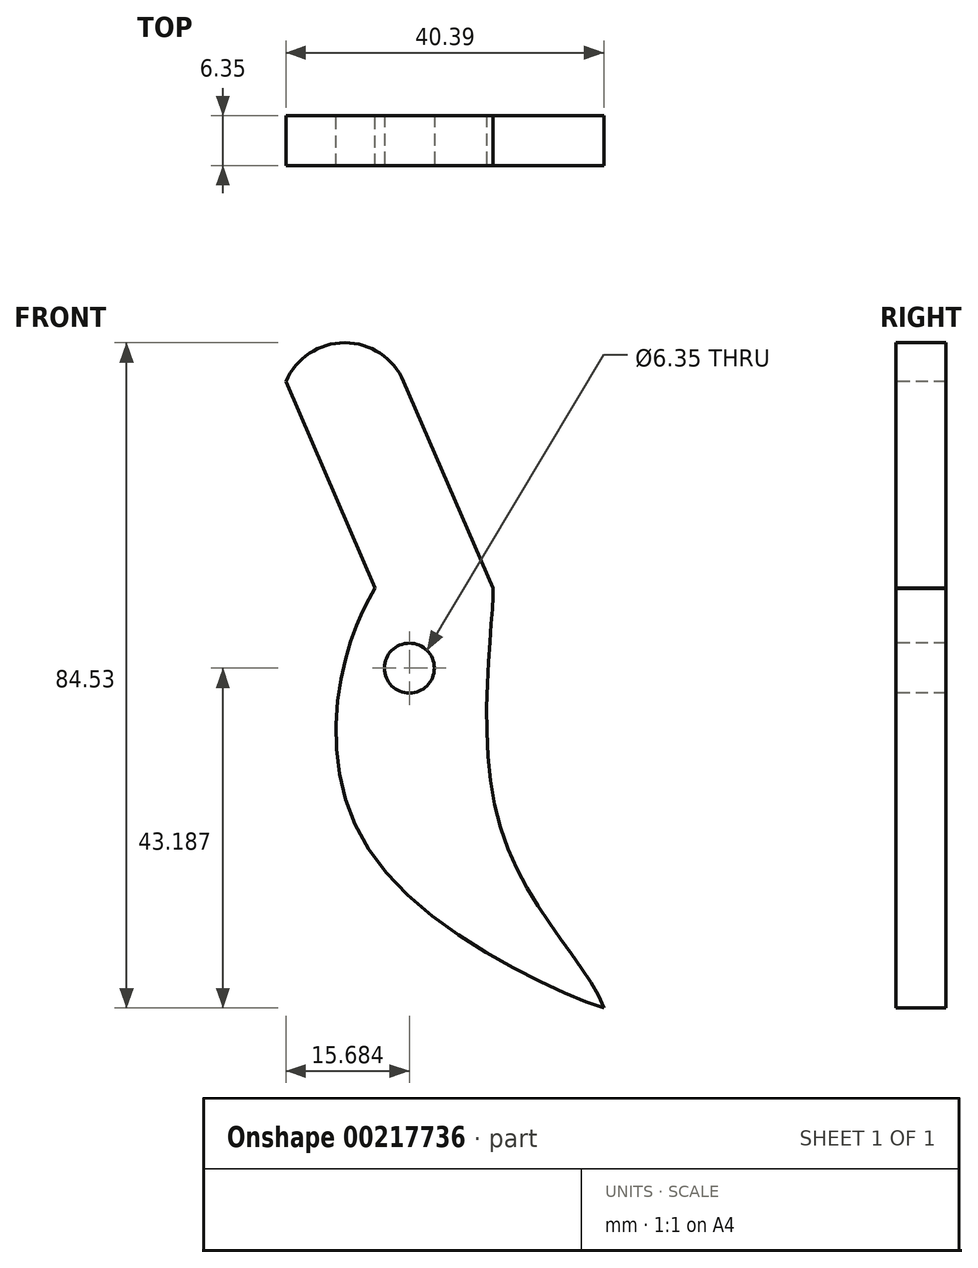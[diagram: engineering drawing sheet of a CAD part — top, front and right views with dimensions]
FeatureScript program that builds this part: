
annotation { "Feature Type Name" : "Feature", "Feature Type Description" : "" }
export const myFeature = defineFeature(function(context is Context, id is Id, definition is map)
    precondition{}
    {
        {
            var Q0;
            Q0=qCreatedBy(makeId("Front.planeOp"),FACE);
            var sketch = newSketch(context, id + "F0", { "sketchPlane" : qUnion([Q0])});
            skLineSegment(sketch, "E0", {"start": v(0, 0) * mm, "end": v(14.98, -0.05) * mm});
            skFitSpline(sketch, "E1", {"points": [v(0, 0) * mm, v(-3.92, -9.7) * mm, v(0, -34.41) * mm, v(29.07, -53.37) * mm], "startDerivative": vector(-17.9, -30.57) * mm, "endDerivative": vector(44.88, -14.69) * mm});
            skFitSpline(sketch, "E2", {"points": [v(14.98, -0.05) * mm, v(15.72, -29.7) * mm, v(29.07, -53.37) * mm], "startDerivative": vector(1.5, -18.65) * mm, "endDerivative": vector(13.35, -36.6) * mm});
            skLineSegment(sketch, "E3", {"start": v(0, 0) * mm, "end": v(14.95, 0) * mm});
            skSolve(sketch);
        }
        {
            var Q0;
            Q0 = qSketchRegion(id + "F0", true);
            extrude(context, id + "F1", {"entities" : qUnion([Q0]), "depth" : 6.35 * mm});
        }
        {
            var Q0;
            Q0=makeQuery(id+"F1.opExtrude","CAP_FACE",FACE,{"disambiguationData":[OSD([sQuery(id+"F0.wireOp",EDGE,"htK93jvt-rHRG-NFRo-RSNv-obEK3Ky7y3zf"),sQuery(id+"F0.wireOp",EDGE,"71433e04-a7d7-4233-bdce-b1169e7c8268"),sQuery(id+"F0.wireOp",EDGE,"E0")])],"isStart":false});
            var sketch = newSketch(context, id + "F2", { "sketchPlane" : qUnion([Q0])});
            skLineSegment(sketch, "E4", {"start": v(0, 0) * mm, "end": v(-11.32, 26.24) * mm});
            skLineSegment(sketch, "E5", {"start": v(14.98, 0) * mm, "end": v(3.65, 26.24) * mm});
            skLineSegment(sketch, "E6", {"start": v(0, 0) * mm, "end": v(0, 0) * mm});
            skArc(sketch, "E7", {"start": v(3.65, 26.24) * mm, "mid": v(-3.84, 31.16) * mm, "end": v(-11.32, 26.24) * mm});
            skLineSegment(sketch, "E8", {"start": v(14.98, 0) * mm, "end": v(14.93, -2.19) * mm});
            skLineSegment(sketch, "E9", {"start": v(14.93, -2.19) * mm, "end": v(1.36, -2.19) * mm});
            skLineSegment(sketch, "E10", {"start": v(1.36, -2.19) * mm, "end": v(0, 0) * mm});
            skSolve(sketch);
        }
        {
            var Q0;
            Q0 = qSketchRegion(id + "F2", true);
            extrude(context, id + "F3", {"entities" : qUnion([Q0]), "operationType" : NewBodyOperationType.ADD, "oppositeDirection" : true, "depth" : 6.35 * mm});
        }
        {
            var Q0;
            Q0=makeQuery(id+"F3.boolean.opBoolean","MERGE",FACE,{"derivedFrom":[makeQuery(id+"F1.opExtrude","CAP_FACE",FACE,{"disambiguationData":[OSD([sQuery(id+"F0.wireOp",EDGE,"htK93jvt-rHRG-NFRo-RSNv-obEK3Ky7y3zf"),sQuery(id+"F0.wireOp",EDGE,"71433e04-a7d7-4233-bdce-b1169e7c8268"),sQuery(id+"F0.wireOp",EDGE,"E0")])],"isStart":false}),makeQuery(id+"F3.opExtrude","CAP_FACE",FACE,{"disambiguationData":[OSD([sQuery(id+"F2.wireOp",EDGE,"E4"),sQuery(id+"F2.wireOp",EDGE,"E5"),sQuery(id+"F2.wireOp",EDGE,"e2af5e4e-8144-4bb3-ac73-6acb8b2ba0d2"),sQuery(id+"F2.wireOp",EDGE,"E6")])],"isStart":true})]});
            var sketch = newSketch(context, id + "F4", { "sketchPlane" : qUnion([Q0])});
            skCircle(sketch, "E11", {"center": v(4.36, -10.18) * mm, "radius": 3.18 * mm});
            skSolve(sketch);
        }
        {
            var Q0;
            Q0 = qSketchRegion(id + "F4", true);
            extrude(context, id + "F5", {"entities" : qUnion([Q0]), "operationType" : NewBodyOperationType.REMOVE, "oppositeDirection" : true, "depth" : 25.4 * mm});
        }
    });
